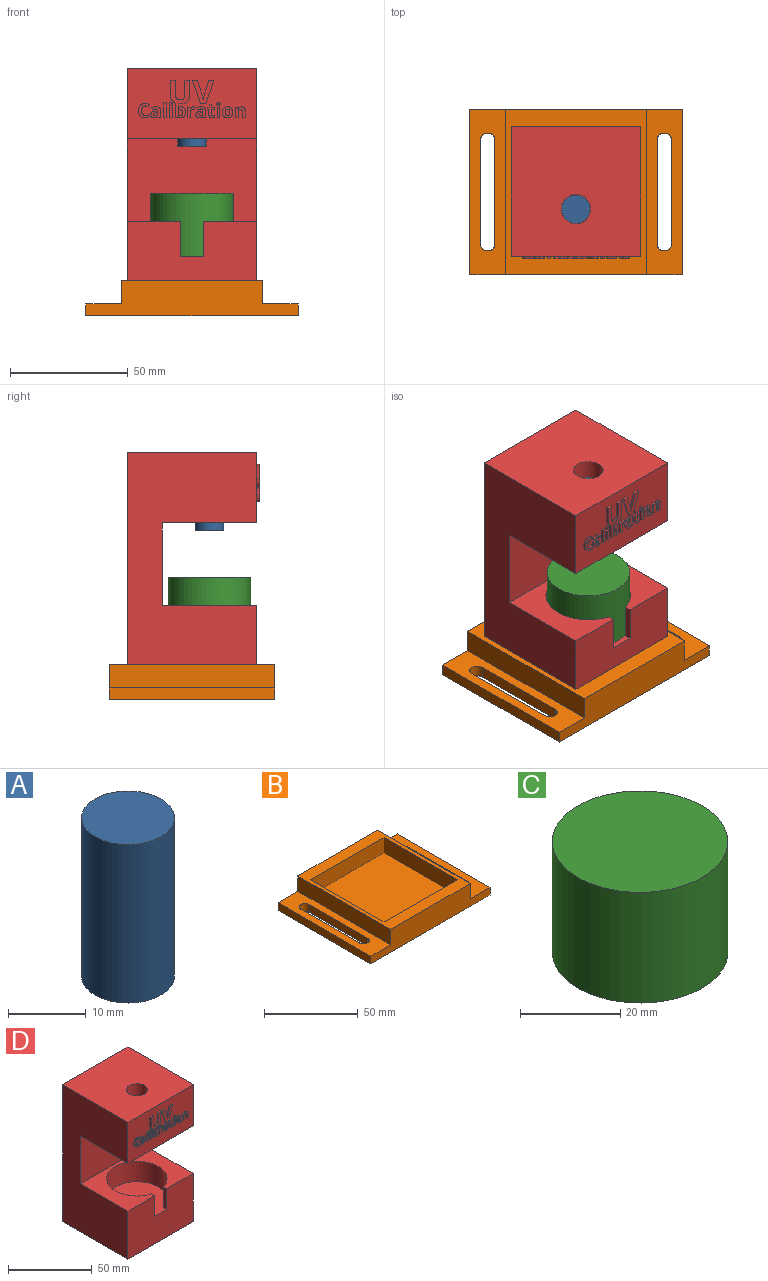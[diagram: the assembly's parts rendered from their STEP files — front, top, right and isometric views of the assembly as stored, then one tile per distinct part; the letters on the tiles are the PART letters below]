
ASSEMBLY  parts=4 mates=7
PART A: 3 faces, bbox 12x12x25 mm
  f0: cylinder r=6mm len=25mm, axis (0,0,-1), area 942.5mm2, adj f1,f2
  f1: plane 12x12mm, normal (0,0,1), area 113.1mm2, adj f0
  f2: plane 12x12mm, normal (0,0,-1), area 113.1mm2, adj f0
PART B: 23 faces, bbox 90x70x15 mm
  f0: plane 70x15mm, normal (0,0,1), area 748.2mm2, adj f2,f3,f5,f10,f15,f16,f17,f18
  f1: plane 90x70mm, normal (0,0,-1), area 5696.5mm2, adj f2,f3,f4,f5,f15,f16,f17,f18
  f2: plane 70x5mm, normal (1,0,0), area 350mm2, adj f0,f1,f3,f5
  f3: plane 90x15mm, normal (0,1,0), area 1050mm2, adj f0,f1,f2,f4,f6,f10,f11,f13
  f4: plane 70x5mm, normal (-1,0,0), area 350mm2, adj f1,f3,f5,f6
  f5: plane 90x15mm, normal (0,-1,0), area 1050mm2, adj f0,f1,f2,f4,f6,f10,f11,f13
  f6: plane 70x15mm, normal (0,0,1), area 748.2mm2, adj f3,f4,f5,f11,f19,f20,f21,f22
  f7: plane 55.1x10mm, normal (0,-1,0), area 551mm2, adj f8,f12,f13,f14
  f8: plane 55.1x10mm, normal (-1,0,0), area 551mm2, adj f7,f9,f13,f14
  f9: plane 55.1x10mm, normal (0,1,0), area 551mm2, adj f8,f12,f13,f14
  f10: plane 70x10mm, normal (1,0,0), area 700mm2, adj f0,f3,f5,f13
  f11: plane 70x10mm, normal (-1,0,0), area 700mm2, adj f3,f5,f6,f13
  f12: plane 55.1x10mm, normal (1,0,0), area 551mm2, adj f7,f9,f13,f14
  f13: plane 70x60mm, normal (0,0,1), area 1164mm2, adj f3,f5,f7,f8,f9,f10,f11,f12
  f14: plane 55.1x55.1mm, normal (0,0,1), area 3036mm2, adj f7,f8,f9,f12
  f15: cylinder r=3.1mm len=6.2mm, axis (0,0,-1), area 48.7mm2, adj f0,f1,f16,f18
  f16: plane 43.8x5mm, normal (1,0,0), area 219mm2, adj f0,f1,f15,f17
  f17: cylinder r=3.1mm len=6.2mm, axis (0,0,-1), area 48.7mm2, adj f0,f1,f16,f18
  f18: plane 43.8x5mm, normal (-1,0,0), area 219mm2, adj f0,f1,f15,f17
  f19: cylinder r=3.1mm len=6.2mm, axis (0,0,-1), area 48.7mm2, adj f1,f6,f20,f22
  f20: plane 43.8x5mm, normal (1,0,0), area 219mm2, adj f1,f6,f19,f21
  f21: cylinder r=3.1mm len=6.2mm, axis (0,0,-1), area 48.7mm2, adj f1,f6,f20,f22
  f22: plane 43.8x5mm, normal (-1,0,0), area 219mm2, adj f1,f6,f19,f21
PART C: 5 faces, bbox 37.5x35x27 mm
  f0: cylinder r=17.5mm len=35mm, axis (0,0,-1), area 2949.1mm2, adj f1,f2,f3
  f1: plane 35x35mm, normal (0,0,1), area 962.1mm2, adj f0
  f2: plane 35x35mm, normal (0,0,-1), area 962.1mm2, adj f0
  f3: cylinder r=2.5mm len=5mm, axis (-1,0,0), area 40.7mm2, adj f0,f4
  f4: plane 5x5mm, normal (1,0,0), area 19.6mm2, adj f3
PART D: 237 faces, bbox 55x56x100 mm
  f0: plane 55x30mm, normal (0,-1,0), area 1438.3mm2, adj f2,f4,f6,f8,f26,f27,f28,f29
  f1: cylinder r=18mm len=36mm, axis (0,0,1), area 1544.5mm2, adj f9,f11,f15,f16
  f2: plane 100x55mm, normal (-1,0,0), area 4100mm2, adj f0,f3,f5,f6,f7,f8,f9,f10
  f3: plane 55x35mm, normal (0,-1,0), area 1775mm2, adj f2,f4,f7,f9,f11,f15,f16
  f4: plane 100x55mm, normal (1,0,0), area 4100mm2, adj f0,f3,f5,f6,f7,f8,f9,f10
  f5: plane 100x55mm, normal (0,1,0), area 5500mm2, adj f2,f4,f6,f7
  f6: plane 55x55mm, normal (0,0,1), area 2902.3mm2, adj f0,f2,f4,f5,f12
  f7: plane 55x55mm, normal (0,0,-1), area 3025mm2, adj f2,f3,f4,f5
  f8: plane 55x40mm, normal (0,0,-1), area 1945.5mm2, adj f0,f2,f4,f10,f17
  f9: plane 55x40mm, normal (0,0,1), area 1159.8mm2, adj f1,f2,f3,f4,f10,f15,f16
  f10: plane 55x35mm, normal (0,-1,0), area 1925mm2, adj f2,f4,f8,f9
  f11: plane 38x36mm, normal (0,0,1), area 1040.2mm2, adj f1,f3,f15,f16
  f12: cylinder r=6.25mm len=20mm, axis (0,0,1), area 785.4mm2, adj f6,f13
  f13: plane 12.5x12.5mm, normal (0,0,1), area 27.7mm2, adj f12,f14
  f14: cylinder r=5.5mm len=11mm, axis (0,0,1), area 224.6mm2, adj f13,f17
  f15: plane 15x2.71mm, normal (1,0,0), area 40.6mm2, adj f1,f3,f9,f11
  f16: plane 15x2.71mm, normal (-1,0,0), area 40.6mm2, adj f1,f3,f9,f11
  f17: cone r=9mm half-angle=45deg, axis (0,0,-1), area 225.5mm2, adj f8,f14
  f18: extruded ~1x0.67mm, area 0.8mm2, adj f19,f55,f56,f57
  f19: extruded ~1x0.62mm, area 0.7mm2, adj f18,f20,f56,f57
  f20: extruded ~1.01x1mm, area 1mm2, adj f19,f21,f56,f57
  f21: extruded ~1.02x1mm, area 1.1mm2, adj f20,f22,f56,f57
  f22: extruded ~1x0.61mm, area 0.7mm2, adj f21,f23,f56,f57
  f23: extruded ~1x0.69mm, area 0.8mm2, adj f22,f24,f56,f57
  f24: extruded ~1.05x1mm, area 1.1mm2, adj f23,f25,f56,f57
  f25: plane 1x0.14mm, normal (1,0,0), area 0.1mm2, adj f24,f55,f56,f57
  f26: extruded ~1x0.94mm, area 1.1mm2, adj f0,f27,f54,f56
  f27: plane 6.24x1mm, normal (-1,0,0), area 6.2mm2, adj f0,f26,f28,f56
  f28: plane 1x0.95mm, normal (0,0,-1), area 0.9mm2, adj f0,f27,f29,f56
  f29: plane 1x0.5mm, normal (0.92,0,-0.38), area 0.5mm2, adj f0,f28,f30,f56
  f30: plane 1x0.08mm, normal (0,0,-1), area 0.1mm2, adj f0,f29,f31,f56
  f31: extruded ~1.26x1mm, area 1.4mm2, adj f0,f30,f32,f56
  f32: extruded ~1.28x1mm, area 1.5mm2, adj f0,f31,f33,f56
  f33: extruded ~1.75x1mm, area 1.8mm2, adj f0,f32,f34,f56
  f34: extruded ~1.72x1mm, area 1.8mm2, adj f0,f33,f35,f56
  f35: extruded ~1.26x1mm, area 1.5mm2, adj f0,f34,f36,f56
  f36: extruded ~1.29x1mm, area 1.5mm2, adj f0,f35,f37,f56
  f37: plane 1x0.05mm, normal (0,0,1), area 0mm2, adj f0,f36,f38,f56
  f38: extruded ~1x0.9mm, area 0.9mm2, adj f0,f37,f39,f56
  f39: plane 1.05x1mm, normal (1,0,0), area 1.1mm2, adj f0,f38,f40,f56
  f40: extruded ~1x0.79mm, area 0.8mm2, adj f0,f39,f41,f56
  f41: extruded ~2.2x1mm, area 2.3mm2, adj f0,f40,f42,f56
  f42: extruded ~1.42x1.27mm, area 1.9mm2, adj f0,f41,f43,f56
  f43: extruded ~1.93x1mm, area 2mm2, adj f0,f42,f44,f56
  f44: plane 6.42x1mm, normal (1,0,0), area 6.4mm2, adj f0,f43,f45,f56
  f45: plane 2.1x1mm, normal (0,0,1), area 2.1mm2, adj f0,f44,f46,f56
  f46: plane 6.06x1mm, normal (-1,0,0), area 6.1mm2, adj f0,f45,f47,f56
  f47: extruded ~1.69x1mm, area 1.8mm2, adj f0,f46,f48,f56
  f48: extruded ~1.5x1mm, area 1.6mm2, adj f0,f47,f49,f56
  f49: extruded ~1.53x1mm, area 1.7mm2, adj f0,f48,f50,f56
  f50: extruded ~1.68x1mm, area 1.8mm2, adj f0,f49,f51,f56
  f51: plane 6.07x1mm, normal (1,0,0), area 6.1mm2, adj f0,f50,f52,f56
  f52: plane 2.09x1mm, normal (0,0,1), area 2.1mm2, adj f0,f51,f53,f56
  f53: plane 6.39x1mm, normal (-1,0,0), area 6.4mm2, adj f0,f52,f54,f56
  f54: extruded ~2.68x1.06mm, area 3mm2, adj f0,f26,f53,f56
  f55: extruded ~1x0.93mm, area 1mm2, adj f18,f25,f56,f57
  f56: plane 16x8.14mm, normal (0,-1,0), area 60.6mm2, adj f18,f19,f20,f21,f22,f23,f24,f25
  f57: plane 2.72x1.74mm, normal (0,-1,0), area 4mm2, adj f18,f19,f20,f21,f22,f23,f24,f25
  f58: plane 2.12x1mm, normal (0,0,1), area 2.1mm2, adj f0,f59,f67,f68
  f59: plane 5.9x1.88mm, normal (-0.95,0,0.3), area 6.2mm2, adj f0,f58,f60,f68
  f60: extruded ~2.18x1mm, area 2.2mm2, adj f0,f59,f61,f68
  f61: extruded ~1x0.97mm, area 1mm2, adj f0,f60,f62,f68
  f62: extruded ~1.22x1mm, area 1.3mm2, adj f0,f61,f63,f68
  f63: plane 5.9x1.87mm, normal (0.95,0,0.3), area 6.2mm2, adj f0,f62,f64,f68
  f64: plane 2.12x1mm, normal (0,0,1), area 2.1mm2, adj f0,f63,f65,f68
  f65: plane 9.92x3.36mm, normal (-0.95,0,-0.32), area 10.5mm2, adj f0,f64,f66,f68
  f66: plane 2.29x1mm, normal (0,0,-1), area 2.3mm2, adj f0,f65,f67,f68
  f67: plane 9.92x3.37mm, normal (0.95,0,-0.32), area 10.5mm2, adj f0,f58,f66,f68
  f68: plane 9.92x9.03mm, normal (0,-1,0), area 37.9mm2, adj f58,f59,f60,f61,f62,f63,f64,f65
  f69: extruded ~1.1x1mm, area 1.3mm2, adj f0,f70,f83,f84
  f70: extruded ~1x0.66mm, area 0.7mm2, adj f0,f69,f71,f84
  f71: extruded ~1x0.67mm, area 0.7mm2, adj f0,f70,f72,f84
  f72: plane 1.03x1mm, normal (0.93,0,-0.37), area 1.1mm2, adj f0,f71,f73,f84
  f73: extruded ~1.74x1mm, area 1.8mm2, adj f0,f72,f74,f84
  f74: extruded ~1.48x1mm, area 1.5mm2, adj f0,f73,f75,f84
  f75: extruded ~1.07x1mm, area 1.5mm2, adj f0,f74,f76,f84
  f76: extruded ~1.63x1mm, area 1.7mm2, adj f0,f75,f77,f84
  f77: extruded ~2.26x1mm, area 2.4mm2, adj f0,f76,f78,f84
  f78: extruded ~1.99x1mm, area 2.2mm2, adj f0,f77,f79,f84
  f79: extruded ~1.64x1mm, area 1.7mm2, adj f0,f78,f80,f84
  f80: plane 1.06x1mm, normal (1,0,0), area 1.1mm2, adj f0,f79,f81,f84
  f81: extruded ~1.52x1mm, area 1.6mm2, adj f0,f80,f82,f84
  f82: extruded ~1.99x1.49mm, area 2.8mm2, adj f0,f81,f83,f84
  f83: extruded ~1.49x1mm, area 1.6mm2, adj f0,f69,f82,f84
  f84: plane 6.12x4.53mm, normal (0,-1,0), area 12.4mm2, adj f69,f70,f71,f72,f73,f74,f75,f76
  f85: plane 1x0.48mm, normal (0.04,0,-1), area 0.5mm2, adj f86,f109,f110,f111
  f86: plane 1x0.38mm, normal (-1,0,0), area 0.4mm2, adj f85,f87,f110,f111
  f87: extruded ~1x0.66mm, area 0.7mm2, adj f86,f88,f110,f111
  f88: extruded ~1x0.69mm, area 0.8mm2, adj f87,f89,f110,f111
  f89: extruded ~1x0.6mm, area 0.9mm2, adj f88,f90,f110,f111
  f90: extruded ~1x0.55mm, area 0.6mm2, adj f89,f109,f110,f111
  f91: plane 1x0.62mm, normal (-0.93,0,-0.36), area 0.7mm2, adj f0,f92,f108,f110
  f92: plane 1x0.87mm, normal (0,0,-1), area 0.9mm2, adj f0,f91,f93,f110
  f93: plane 3.03x1mm, normal (1,0,0), area 3mm2, adj f0,f92,f94,f110
  f94: extruded ~1.21x1mm, area 1.4mm2, adj f0,f93,f95,f110
  f95: extruded ~1.4x1mm, area 1.5mm2, adj f0,f94,f96,f110
  f96: extruded ~1.74x1mm, area 1.8mm2, adj f0,f95,f97,f110
  f97: plane 1x0.84mm, normal (-0.9,0,-0.44), area 0.9mm2, adj f0,f96,f98,f110
  f98: extruded ~1.28x1mm, area 1.3mm2, adj f0,f97,f99,f110
  f99: extruded ~1x0.71mm, area 1.1mm2, adj f0,f98,f100,f110
  f100: plane 1x0.2mm, normal (-1,0,0), area 0.2mm2, adj f0,f99,f101,f110
  f101: plane 1x0.79mm, normal (-0.03,0,1), area 0.8mm2, adj f0,f100,f102,f110
  f102: extruded ~1.53x1mm, area 1.6mm2, adj f0,f101,f103,f110
  f103: extruded ~1.07x1mm, area 1.2mm2, adj f0,f102,f104,f110
  f104: extruded ~1.07x1mm, area 1.2mm2, adj f0,f103,f105,f110
  f105: extruded ~1.03x1mm, area 1.1mm2, adj f0,f104,f106,f110
  f106: extruded ~1x0.86mm, area 0.9mm2, adj f0,f105,f107,f110
  f107: extruded ~1x0.64mm, area 0.9mm2, adj f0,f106,f108,f110
  f108: plane 1x0.03mm, normal (0,0,-1), area 0mm2, adj f0,f91,f107,f110
  f109: extruded ~1x0.81mm, area 0.8mm2, adj f85,f90,f110,f111
  f110: plane 4.73x4.06mm, normal (0,-1,0), area 12.7mm2, adj f85,f86,f87,f88,f89,f90,f91,f92
  f111: plane 1.55x1.28mm, normal (0,-1,0), area 1.6mm2, adj f85,f86,f87,f88,f89,f90,f109
  f112: plane 1.24x1mm, normal (0,0,-1), area 1.2mm2, adj f0,f113,f115,f116
  f113: plane 6.33x1mm, normal (1,0,0), area 6.3mm2, adj f0,f112,f114,f116
  f114: plane 1.24x1mm, normal (0,0,1), area 1.2mm2, adj f0,f113,f115,f116
  f115: plane 6.33x1mm, normal (-1,0,0), area 6.3mm2, adj f0,f112,f114,f116
  f116: plane 6.33x1.24mm, normal (0,-1,0), area 7.9mm2, adj f112,f113,f114,f115
  f117: extruded ~1x0.68mm, area 1mm2, adj f0,f118,f121,f122
  f118: extruded ~1x0.68mm, area 1mm2, adj f0,f117,f119,f122
  f119: extruded ~1x0.51mm, area 0.5mm2, adj f0,f118,f120,f122
  f120: extruded ~1x0.45mm, area 0.5mm2, adj f0,f119,f121,f122
  f121: extruded ~1x0.68mm, area 1mm2, adj f0,f117,f120,f122
  f122: plane 1.35x1.22mm, normal (0,-1,0), area 1.4mm2, adj f117,f118,f119,f120,f121
  f123: plane 1.24x1mm, normal (0,0,-1), area 1.2mm2, adj f0,f124,f126,f127
  f124: plane 4.55x1mm, normal (1,0,0), area 4.5mm2, adj f0,f123,f125,f127
  f125: plane 1.24x1mm, normal (0,0,1), area 1.2mm2, adj f0,f124,f126,f127
  f126: plane 4.55x1mm, normal (-1,0,0), area 4.5mm2, adj f0,f123,f125,f127
  f127: plane 4.55x1.24mm, normal (0,-1,0), area 5.6mm2, adj f123,f124,f125,f126
  f128: extruded ~1x0.42mm, area 0.4mm2, adj f0,f129,f140,f141
  f129: extruded ~1x0.78mm, area 0.8mm2, adj f0,f128,f130,f141
  f130: extruded ~1x0.62mm, area 0.8mm2, adj f0,f129,f131,f141
  f131: plane 1x0.06mm, normal (0,0,1), area 0.1mm2, adj f0,f130,f132,f141
  f132: plane 1x0.77mm, normal (0.97,0,0.23), area 0.8mm2, adj f0,f131,f133,f141
  f133: plane 1x0.94mm, normal (0,0,1), area 0.9mm2, adj f0,f132,f134,f141
  f134: plane 4.55x1mm, normal (-1,0,0), area 4.5mm2, adj f0,f133,f135,f141
  f135: plane 1.24x1mm, normal (0,0,-1), area 1.2mm2, adj f0,f134,f136,f141
  f136: plane 2.32x1mm, normal (1,0,0), area 2.3mm2, adj f0,f135,f137,f141
  f137: extruded ~1x0.86mm, area 0.9mm2, adj f0,f136,f138,f141
  f138: extruded ~1x0.93mm, area 1mm2, adj f0,f137,f139,f141
  f139: extruded ~1x0.37mm, area 0.4mm2, adj f0,f138,f140,f141
  f140: plane 1.16x1mm, normal (1,0,-0.08), area 1.2mm2, adj f0,f128,f139,f141
  f141: plane 4.63x2.96mm, normal (0,-1,0), area 7.4mm2, adj f128,f129,f130,f131,f132,f133,f134,f135
  f142: plane 1x0.48mm, normal (0.04,0,-1), area 0.5mm2, adj f143,f166,f167,f168
  f143: plane 1x0.38mm, normal (-1,0,0), area 0.4mm2, adj f142,f144,f167,f168
  f144: extruded ~1x0.66mm, area 0.7mm2, adj f143,f145,f167,f168
  f145: extruded ~1x0.69mm, area 0.8mm2, adj f144,f146,f167,f168
  f146: extruded ~1x0.6mm, area 0.9mm2, adj f145,f147,f167,f168
  f147: extruded ~1x0.55mm, area 0.6mm2, adj f146,f166,f167,f168
  f148: plane 1x0.62mm, normal (-0.93,0,-0.36), area 0.7mm2, adj f0,f149,f165,f167
  f149: plane 1x0.87mm, normal (0,0,-1), area 0.9mm2, adj f0,f148,f150,f167
  f150: plane 3.03x1mm, normal (1,0,0), area 3mm2, adj f0,f149,f151,f167
  f151: extruded ~1.21x1mm, area 1.4mm2, adj f0,f150,f152,f167
  f152: extruded ~1.4x1mm, area 1.5mm2, adj f0,f151,f153,f167
  f153: extruded ~1.74x1mm, area 1.8mm2, adj f0,f152,f154,f167
  f154: plane 1x0.84mm, normal (-0.9,0,-0.44), area 0.9mm2, adj f0,f153,f155,f167
  f155: extruded ~1.28x1mm, area 1.3mm2, adj f0,f154,f156,f167
  f156: extruded ~1x0.71mm, area 1.1mm2, adj f0,f155,f157,f167
  f157: plane 1x0.2mm, normal (-1,0,0), area 0.2mm2, adj f0,f156,f158,f167
  f158: plane 1x0.79mm, normal (-0.03,0,1), area 0.8mm2, adj f0,f157,f159,f167
  f159: extruded ~1.53x1mm, area 1.6mm2, adj f0,f158,f160,f167
  f160: extruded ~1.07x1mm, area 1.2mm2, adj f0,f159,f161,f167
  f161: extruded ~1.07x1mm, area 1.2mm2, adj f0,f160,f162,f167
  f162: extruded ~1.03x1mm, area 1.1mm2, adj f0,f161,f163,f167
  f163: extruded ~1x0.86mm, area 0.9mm2, adj f0,f162,f164,f167
  f164: extruded ~1x0.64mm, area 0.9mm2, adj f0,f163,f165,f167
  f165: plane 1x0.03mm, normal (0,0,-1), area 0mm2, adj f0,f148,f164,f167
  f166: extruded ~1x0.81mm, area 0.8mm2, adj f142,f147,f167,f168
  f167: plane 4.73x4.06mm, normal (0,-1,0), area 12.7mm2, adj f142,f143,f144,f145,f146,f147,f148,f149
  f168: plane 1.55x1.28mm, normal (0,-1,0), area 1.6mm2, adj f142,f143,f144,f145,f146,f147,f166
  f169: extruded ~1x0.78mm, area 0.8mm2, adj f0,f170,f186,f187
  f170: extruded ~1x0.39mm, area 0.4mm2, adj f0,f169,f171,f187
  f171: extruded ~1x0.39mm, area 0.4mm2, adj f0,f170,f172,f187
  f172: plane 2.19x1mm, normal (1,0,0), area 2.2mm2, adj f0,f171,f173,f187
  f173: plane 1.27x1mm, normal (0,0,-1), area 1.3mm2, adj f0,f172,f174,f187
  f174: plane 1x0.93mm, normal (1,0,0), area 0.9mm2, adj f0,f173,f175,f187
  f175: plane 1.27x1mm, normal (0,0,1), area 1.3mm2, adj f0,f174,f176,f187
  f176: plane 1x0.97mm, normal (1,0,0), area 1mm2, adj f0,f175,f177,f187
  f177: plane 1x0.79mm, normal (0,0,1), area 0.8mm2, adj f0,f176,f178,f187
  f178: plane 1x0.96mm, normal (-0.94,0,0.35), area 1mm2, adj f0,f177,f179,f187
  f179: plane 1x0.68mm, normal (-0.52,0,0.85), area 0.8mm2, adj f0,f178,f180,f187
  f180: plane 1x0.52mm, normal (-1,0,0), area 0.5mm2, adj f0,f179,f181,f187
  f181: plane 1x0.59mm, normal (0,0,-1), area 0.6mm2, adj f0,f180,f182,f187
  f182: plane 2.19x1mm, normal (-1,0,0), area 2.2mm2, adj f0,f181,f183,f187
  f183: extruded ~1.13x1mm, area 1.2mm2, adj f0,f182,f184,f187
  f184: extruded ~1.08x1mm, area 1.2mm2, adj f0,f183,f185,f187
  f185: extruded ~1.14x1mm, area 1.2mm2, adj f0,f184,f186,f187
  f186: plane 1x0.92mm, normal (1,0,0), area 0.9mm2, adj f0,f169,f185,f187
  f187: plane 5.6x3.16mm, normal (0,-1,0), area 9.3mm2, adj f169,f170,f171,f172,f173,f174,f175,f176
  f188: extruded ~1x0.68mm, area 1mm2, adj f0,f189,f192,f193
  f189: extruded ~1x0.68mm, area 1mm2, adj f0,f188,f190,f193
  f190: extruded ~1x0.51mm, area 0.5mm2, adj f0,f189,f191,f193
  f191: extruded ~1x0.45mm, area 0.5mm2, adj f0,f190,f192,f193
  f192: extruded ~1x0.68mm, area 1mm2, adj f0,f188,f191,f193
  f193: plane 1.35x1.22mm, normal (0,-1,0), area 1.4mm2, adj f188,f189,f190,f191,f192
  f194: plane 1.24x1mm, normal (0,0,-1), area 1.2mm2, adj f0,f195,f197,f198
  f195: plane 4.55x1mm, normal (1,0,0), area 4.5mm2, adj f0,f194,f196,f198
  f196: plane 1.24x1mm, normal (0,0,1), area 1.2mm2, adj f0,f195,f197,f198
  f197: plane 4.55x1mm, normal (-1,0,0), area 4.5mm2, adj f0,f194,f196,f198
  f198: plane 4.55x1.24mm, normal (0,-1,0), area 5.6mm2, adj f194,f195,f196,f197
  f199: extruded ~1.74x1mm, area 1.9mm2, adj f0,f200,f216,f217
  f200: extruded ~1.25x1mm, area 1.3mm2, adj f0,f199,f201,f217
  f201: extruded ~1x0.82mm, area 1.1mm2, adj f0,f200,f202,f217
  f202: extruded ~1.16x1mm, area 1.2mm2, adj f0,f201,f203,f217
  f203: extruded ~1.64x1mm, area 1.8mm2, adj f0,f202,f204,f217
  f204: extruded ~1.73x1mm, area 1.9mm2, adj f0,f203,f205,f217
  f205: extruded ~1.25x1mm, area 1.3mm2, adj f0,f204,f206,f217
  f206: extruded ~1x0.82mm, area 1.1mm2, adj f0,f205,f207,f217
  f207: extruded ~1.16x1mm, area 1.2mm2, adj f0,f206,f216,f217
  f208: extruded ~1.02x1mm, area 1.1mm2, adj f209,f215,f217,f218
  f209: extruded ~1.02x1mm, area 1.1mm2, adj f208,f210,f217,f218
  f210: extruded ~1x0.72mm, area 0.8mm2, adj f209,f211,f217,f218
  f211: extruded ~1x0.72mm, area 0.8mm2, adj f210,f212,f217,f218
  f212: extruded ~1.01x1mm, area 1.1mm2, adj f211,f213,f217,f218
  f213: extruded ~1.02x1mm, area 1.1mm2, adj f212,f214,f217,f218
  f214: extruded ~1x0.72mm, area 0.8mm2, adj f213,f215,f217,f218
  f215: extruded ~1x0.72mm, area 0.8mm2, adj f208,f214,f217,f218
  f216: extruded ~1.63x1mm, area 1.8mm2, adj f0,f199,f207,f217
  f217: plane 4.72x4.41mm, normal (0,-1,0), area 12.7mm2, adj f199,f200,f201,f202,f203,f204,f205,f206
  f218: plane 2.72x1.88mm, normal (0,-1,0), area 4.3mm2, adj f208,f209,f210,f211,f212,f213,f214,f215
  f219: plane 1.24x1mm, normal (0,0,-1), area 1.2mm2, adj f0,f220,f235,f236
  f220: plane 2.97x1mm, normal (1,0,0), area 3mm2, adj f0,f219,f221,f236
  f221: extruded ~1.24x1mm, area 1.3mm2, adj f0,f220,f222,f236
  f222: extruded ~1.21x1mm, area 1.3mm2, adj f0,f221,f223,f236
  f223: extruded ~1x0.83mm, area 0.9mm2, adj f0,f222,f224,f236
  f224: extruded ~1x0.57mm, area 0.8mm2, adj f0,f223,f225,f236
  f225: plane 1x0.07mm, normal (0,0,1), area 0.1mm2, adj f0,f224,f226,f236
  f226: plane 1x0.58mm, normal (0.96,0,0.28), area 0.6mm2, adj f0,f225,f227,f236
  f227: plane 1x0.95mm, normal (0,0,1), area 0.9mm2, adj f0,f226,f228,f236
  f228: plane 4.55x1mm, normal (-1,0,0), area 4.5mm2, adj f0,f227,f229,f236
  f229: plane 1.24x1mm, normal (0,0,-1), area 1.2mm2, adj f0,f228,f230,f236
  f230: plane 2.14x1mm, normal (1,0,0), area 2.1mm2, adj f0,f229,f231,f236
  f231: extruded ~1.15x1mm, area 1.2mm2, adj f0,f230,f232,f236
  f232: extruded ~1x0.75mm, area 0.9mm2, adj f0,f231,f233,f236
  f233: extruded ~1x0.56mm, area 0.6mm2, adj f0,f232,f234,f236
  f234: extruded ~1x0.74mm, area 0.8mm2, adj f0,f233,f235,f236
  f235: plane 2.66x1mm, normal (-1,0,0), area 2.7mm2, adj f0,f219,f234,f236
  f236: plane 4.63x4.2mm, normal (0,-1,0), area 12.6mm2, adj f219,f220,f221,f222,f223,f224,f225,f226
PLACE A rot(axis=(0.99,-0.12,0),180deg) t=(-13.12,-66.23,40.87)mm
PLACE B rot(axis=(1,0,0),0deg) t=(-13.07,-58.78,-56.13)mm
PLACE C rot(axis=(0,0,-1),14.3deg) t=(-13.12,-66.23,-31.13)mm
PLACE D rot(axis=(1,0,0),0deg) t=(-13.12,-58.73,-51.13)mm
MATE cylindrical A.f0 <-> D.f1  axis (0,0,1) through (-13.12,-66.23,28.37)mm
MATE planar B.f7 <-> D.f5  axis (0,-1,0) through (-13.07,-31.23,-46.13)mm
MATE planar D.f11 <-> C.f0  axis (0,0,1) through (-13.12,-66.63,-31.13)mm
MATE planar D.f2 <-> B.f12  axis (-1,0,0) through (-40.62,-66.23,-16.13)mm
MATE planar B.f14 <-> D.f7  axis (0,0,1) through (-13.07,-58.78,-51.13)mm
MATE planar C.f0 <-> A.f0  axis (0,0,1) through (-13.12,-66.23,-4.13)mm
MATE cylindrical D.f1 <-> C.f0  axis (0,0,1) through (-13.12,-66.23,-23.63)mm
